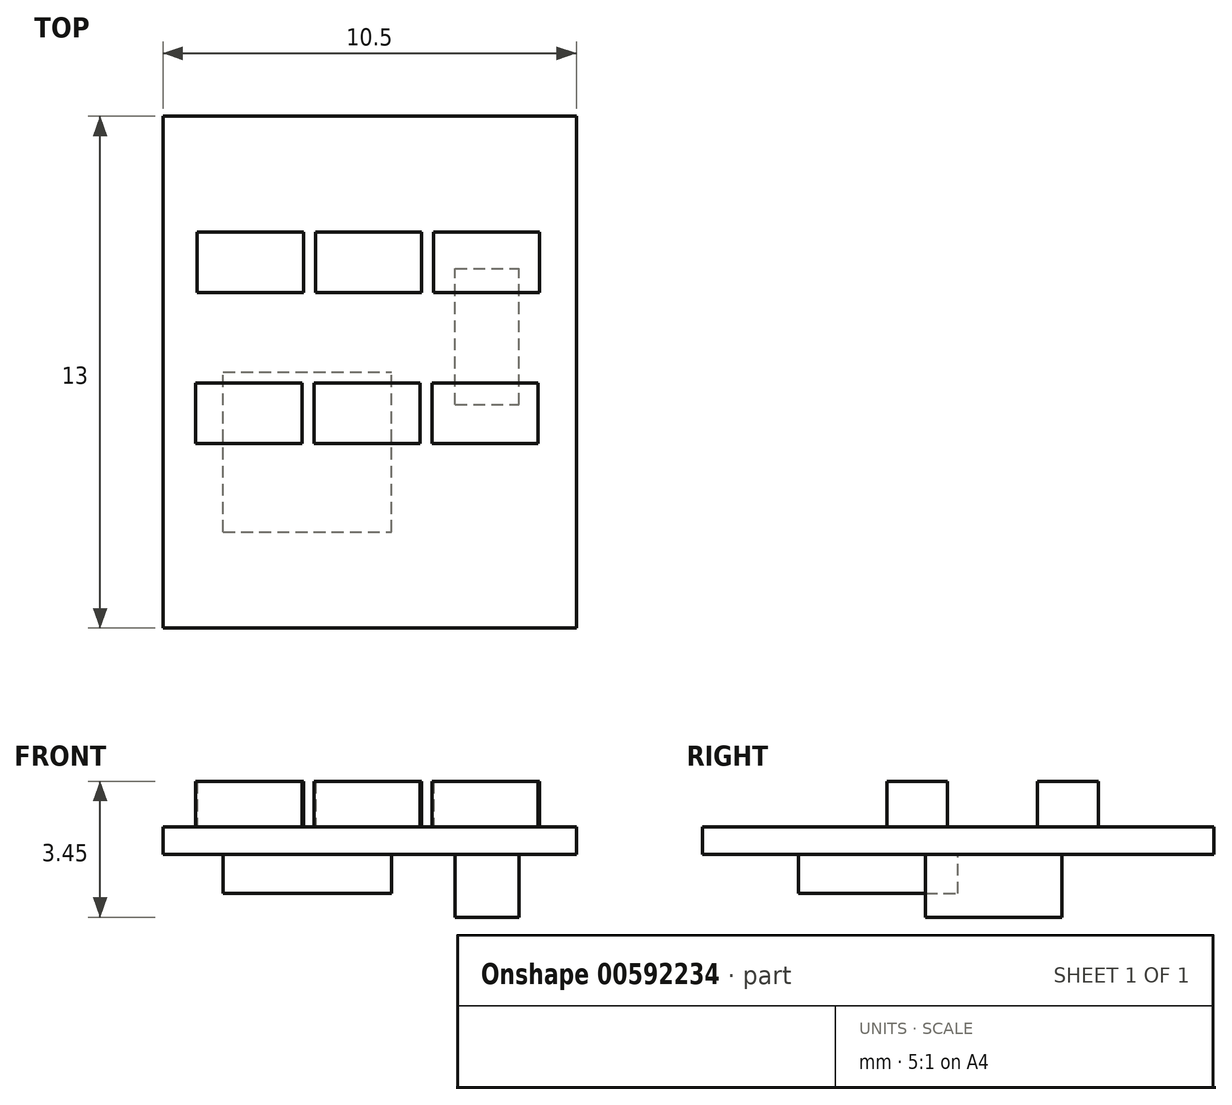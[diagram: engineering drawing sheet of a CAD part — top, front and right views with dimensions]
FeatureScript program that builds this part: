
annotation { "Feature Type Name" : "Feature", "Feature Type Description" : "" }
export const myFeature = defineFeature(function(context is Context, id is Id, definition is map)
    precondition{}
    {
        {
            var Q0;
            Q0=qCreatedBy(makeId("Top.planeOp"),FACE);
            var sketch = newSketch(context, id + "F0", { "sketchPlane" : qUnion([Q0])});
            skLineSegment(sketch, "E0.bottom", {"start": v(-5.25, 6.5) * mm, "end": v(5.25, 6.5) * mm});
            skLineSegment(sketch, "E0.top", {"start": v(-5.25, -6.5) * mm, "end": v(5.25, -6.5) * mm});
            skLineSegment(sketch, "E0.left", {"start": v(-5.25, 6.5) * mm, "end": v(-5.25, -6.5) * mm});
            skLineSegment(sketch, "E0.right", {"start": v(5.25, 6.5) * mm, "end": v(5.25, -6.5) * mm});
            skPoint(sketch, "E0.middle", {"position": v(0, 0) * mm});
            skLineSegment(sketch, "E1.bottom", {"start": v(-4.38, 3.56) * mm, "end": v(-1.68, 3.56) * mm});
            skLineSegment(sketch, "E1.top", {"start": v(-4.38, 2.02) * mm, "end": v(-1.68, 2.02) * mm});
            skLineSegment(sketch, "E1.left", {"start": v(-4.38, 3.56) * mm, "end": v(-4.38, 2.02) * mm});
            skLineSegment(sketch, "E1.right", {"start": v(-1.68, 3.56) * mm, "end": v(-1.68, 2.02) * mm});
            skLineSegment(sketch, "E2.1.0.0", {"start": v(-1.38, 3.56) * mm, "end": v(1.32, 3.56) * mm});
            skLineSegment(sketch, "E2.1.0.1", {"start": v(-1.38, 3.56) * mm, "end": v(-1.38, 2.02) * mm});
            skLineSegment(sketch, "E2.1.0.2", {"start": v(1.32, 3.56) * mm, "end": v(1.32, 2.02) * mm});
            skLineSegment(sketch, "E2.1.0.3", {"start": v(-1.38, 2.02) * mm, "end": v(1.32, 2.02) * mm});
            skLineSegment(sketch, "E2.2.0.0", {"start": v(1.62, 3.56) * mm, "end": v(4.32, 3.56) * mm});
            skLineSegment(sketch, "E2.2.0.1", {"start": v(1.62, 3.56) * mm, "end": v(1.62, 2.02) * mm});
            skLineSegment(sketch, "E2.2.0.2", {"start": v(4.32, 3.56) * mm, "end": v(4.32, 2.02) * mm});
            skLineSegment(sketch, "E2.2.0.3", {"start": v(1.62, 2.02) * mm, "end": v(4.32, 2.02) * mm});
            skLineSegment(sketch, "E2.direction1", {"start": v(-4.38, 3.56) * mm, "end": v(-1.38, 3.56) * mm, "construction": true});
            skLineSegment(sketch, "E3.1.0.0", {"start": v(-4.42, -0.27) * mm, "end": v(-4.42, -1.81) * mm});
            skLineSegment(sketch, "E3.1.0.1", {"start": v(-4.42, -1.81) * mm, "end": v(-1.72, -1.81) * mm});
            skLineSegment(sketch, "E3.1.0.2", {"start": v(4.28, -0.27) * mm, "end": v(4.28, -1.81) * mm});
            skLineSegment(sketch, "E3.1.0.3", {"start": v(1.58, -1.81) * mm, "end": v(4.28, -1.81) * mm});
            skLineSegment(sketch, "E3.1.0.4", {"start": v(1.58, -0.27) * mm, "end": v(1.58, -1.81) * mm});
            skLineSegment(sketch, "E3.1.0.5", {"start": v(-1.72, -0.27) * mm, "end": v(-1.72, -1.81) * mm});
            skLineSegment(sketch, "E3.1.0.6", {"start": v(-1.42, -0.27) * mm, "end": v(1.28, -0.27) * mm});
            skLineSegment(sketch, "E3.1.0.7", {"start": v(-1.42, -0.27) * mm, "end": v(-1.42, -1.81) * mm});
            skLineSegment(sketch, "E3.1.0.8", {"start": v(1.28, -0.27) * mm, "end": v(1.28, -1.81) * mm});
            skLineSegment(sketch, "E3.1.0.9", {"start": v(-1.42, -1.81) * mm, "end": v(1.28, -1.81) * mm});
            skLineSegment(sketch, "E3.1.0.10", {"start": v(1.58, -0.27) * mm, "end": v(4.28, -0.27) * mm});
            skLineSegment(sketch, "E3.1.0.11", {"start": v(-4.42, -0.27) * mm, "end": v(-1.42, -0.27) * mm, "construction": true});
            skLineSegment(sketch, "E3.1.0.12", {"start": v(-4.42, -0.27) * mm, "end": v(-1.72, -0.27) * mm});
            skLineSegment(sketch, "E3.direction1", {"start": v(-4.38, 2.02) * mm, "end": v(-4.42, -1.81) * mm, "construction": true});
            skSolve(sketch);
        }
        {
            var Q0;
            Q0=makeQuery(id+"F0.imprint","IMPRINT",FACE,{"disambiguationData":[TD([[makeQuery(id+"F0.imprint","IMPRINT",EDGE,{"derivedFrom":sQuery(id+"F0.wireOp",EDGE,"E0.bottom")}),-1.0]])]});
            var Q1;
            Q1=makeQuery(id+"F0.imprint","IMPRINT",FACE,{"disambiguationData":[TD([[makeQuery(id+"F0.imprint","IMPRINT",EDGE,{"derivedFrom":sQuery(id+"F0.wireOp",EDGE,"E3.1.0.0")}),1.0]])]});
            var Q2;
            Q2=makeQuery(id+"F0.imprint","IMPRINT",FACE,{"disambiguationData":[TD([[makeQuery(id+"F0.imprint","IMPRINT",EDGE,{"derivedFrom":sQuery(id+"F0.wireOp",EDGE,"E1.bottom")}),-1.0]])]});
            var Q3;
            Q3=makeQuery(id+"F0.imprint","IMPRINT",FACE,{"disambiguationData":[TD([[makeQuery(id+"F0.imprint","IMPRINT",EDGE,{"derivedFrom":sQuery(id+"F0.wireOp",EDGE,"E2.1.0.0")}),-1.0]])]});
            var Q4;
            Q4=makeQuery(id+"F0.imprint","IMPRINT",FACE,{"disambiguationData":[TD([[makeQuery(id+"F0.imprint","IMPRINT",EDGE,{"derivedFrom":sQuery(id+"F0.wireOp",EDGE,"E3.1.0.6")}),-1.0]])]});
            var Q5;
            Q5=makeQuery(id+"F0.imprint","IMPRINT",FACE,{"disambiguationData":[TD([[makeQuery(id+"F0.imprint","IMPRINT",EDGE,{"derivedFrom":sQuery(id+"F0.wireOp",EDGE,"E3.1.0.2")}),-1.0]])]});
            var Q6;
            Q6=makeQuery(id+"F0.imprint","IMPRINT",FACE,{"disambiguationData":[TD([[makeQuery(id+"F0.imprint","IMPRINT",EDGE,{"derivedFrom":sQuery(id+"F0.wireOp",EDGE,"E2.2.0.0")}),-1.0]])]});
            extrude(context, id + "F1", {"entities" : qUnion([Q0, Q1, Q2, Q3, Q4, Q5, Q6]), "depth" : 0.7 * mm, "offsetDistance" : 25 * mm});
        }
        {
            var Q0;
            Q0=makeQuery(id+"F0.imprint","IMPRINT",FACE,{"disambiguationData":[TD([[makeQuery(id+"F0.imprint","IMPRINT",EDGE,{"derivedFrom":sQuery(id+"F0.wireOp",EDGE,"E3.1.0.0")}),1.0]])]});
            var Q1;
            Q1=makeQuery(id+"F0.imprint","IMPRINT",FACE,{"disambiguationData":[TD([[makeQuery(id+"F0.imprint","IMPRINT",EDGE,{"derivedFrom":sQuery(id+"F0.wireOp",EDGE,"E3.1.0.6")}),-1.0]])]});
            var Q2;
            Q2=makeQuery(id+"F0.imprint","IMPRINT",FACE,{"disambiguationData":[TD([[makeQuery(id+"F0.imprint","IMPRINT",EDGE,{"derivedFrom":sQuery(id+"F0.wireOp",EDGE,"E3.1.0.2")}),-1.0]])]});
            var Q3;
            Q3=makeQuery(id+"F0.imprint","IMPRINT",FACE,{"disambiguationData":[TD([[makeQuery(id+"F0.imprint","IMPRINT",EDGE,{"derivedFrom":sQuery(id+"F0.wireOp",EDGE,"E2.2.0.0")}),-1.0]])]});
            var Q4;
            Q4=makeQuery(id+"F0.imprint","IMPRINT",FACE,{"disambiguationData":[TD([[makeQuery(id+"F0.imprint","IMPRINT",EDGE,{"derivedFrom":sQuery(id+"F0.wireOp",EDGE,"E2.1.0.0")}),-1.0]])]});
            var Q5;
            Q5=makeQuery(id+"F0.imprint","IMPRINT",FACE,{"disambiguationData":[TD([[makeQuery(id+"F0.imprint","IMPRINT",EDGE,{"derivedFrom":sQuery(id+"F0.wireOp",EDGE,"E1.bottom")}),-1.0]])]});
            extrude(context, id + "F2", {"entities" : qUnion([Q0, Q1, Q2, Q3, Q4, Q5]), "operationType" : NewBodyOperationType.ADD, "depth" : 1.85 * mm, "offsetDistance" : 25 * mm});
        }
        {
            var Q0;
            Q0=makeQuery(id+"F0.imprint","IMPRINT",FACE,{"disambiguationData":[TD([[makeQuery(id+"F0.imprint","IMPRINT",EDGE,{"derivedFrom":sQuery(id+"F0.wireOp",EDGE,"E0.bottom")}),-1.0]])]});
            var sketch = newSketch(context, id + "F3", { "sketchPlane" : qUnion([Q0])});
            skLineSegment(sketch, "E4.bottom", {"start": v(-3.72, -4.06) * mm, "end": v(0.56, -4.06) * mm});
            skLineSegment(sketch, "E4.top", {"start": v(-3.72, 0) * mm, "end": v(0.56, 0) * mm});
            skLineSegment(sketch, "E4.left", {"start": v(-3.72, -4.06) * mm, "end": v(-3.72, 0) * mm});
            skLineSegment(sketch, "E4.right", {"start": v(0.56, -4.06) * mm, "end": v(0.56, 0) * mm});
            skLineSegment(sketch, "E5.bottom", {"start": v(2.17, -0.83) * mm, "end": v(3.8, -0.83) * mm});
            skLineSegment(sketch, "E5.top", {"start": v(2.17, 2.63) * mm, "end": v(3.8, 2.63) * mm});
            skLineSegment(sketch, "E5.left", {"start": v(2.17, -0.83) * mm, "end": v(2.17, 2.63) * mm});
            skLineSegment(sketch, "E5.right", {"start": v(3.8, -0.83) * mm, "end": v(3.8, 2.63) * mm});
            skSolve(sketch);
        }
        {
            var Q0;
            {var subQ9=sQuery(id+"F3.wireOp",EDGE,"E4.bottom");Q0=makeQuery(id+"F3.imprint","IMPRINT",FACE,{"disambiguationData":[TD([[makeQuery(id+"F3.imprint","IMPRINT",EDGE,{"derivedFrom":subQ9}),1.0]])]});}
            var Q1;
            {var subQ5=makeQuery(id+"F0.imprint","IMPRINT",EDGE,{"derivedFrom":sQuery(id+"F0.wireOp",EDGE,"E3.1.0.7")});Q1=makeQuery(id+"F3.imprint","IMPRINT",FACE,{"disambiguationData":[TD([[makeQuery(id+"F3.imprint","IMPRINT",EDGE,{"derivedFrom":subQ5}),1.0]])]});}
            var Q2;
            {var subQ5=makeQuery(id+"F0.imprint","IMPRINT",EDGE,{"derivedFrom":sQuery(id+"F0.wireOp",EDGE,"E3.1.0.5")});Q2=makeQuery(id+"F3.imprint","IMPRINT",FACE,{"disambiguationData":[TD([[makeQuery(id+"F3.imprint","IMPRINT",EDGE,{"derivedFrom":subQ5}),-1.0]])]});}
            extrude(context, id + "F4", {"entities" : qUnion([Q0, Q1, Q2]), "operationType" : NewBodyOperationType.ADD, "oppositeDirection" : true, "depth" : 1 * mm, "offsetDistance" : 25 * mm});
        }
        {
            var Q0;
            {var subQ0=sQuery(id+"F3.wireOp",EDGE,"E5.bottom");Q0=makeQuery(id+"F3.imprint","IMPRINT",FACE,{"disambiguationData":[TD([[makeQuery(id+"F3.imprint","IMPRINT",EDGE,{"derivedFrom":subQ0}),1.0]])]});}
            var Q1;
            {var subQ0=sQuery(id+"F3.wireOp",EDGE,"E5.left");var subQ1=makeQuery(id+"F0.imprint","IMPRINT",EDGE,{"derivedFrom":sQuery(id+"F0.wireOp",EDGE,"E3.1.0.10")});var subQ2=makeQuery(id+"F3.imprint","INTERSECT",VERTEX,{"derivedFrom":[subQ1,subQ0]});Q1=makeQuery(id+"F3.imprint","IMPRINT",FACE,{"disambiguationData":[TD([[makeQuery(id+"F3.imprint","IMPRINT",EDGE,{"disambiguationData":[TD([[subQ2,-1.0]])],"derivedFrom":subQ0}),-1.0]])]});}
            var Q2;
            {var subQ0=sQuery(id+"F3.wireOp",EDGE,"E5.top");Q2=makeQuery(id+"F3.imprint","IMPRINT",FACE,{"disambiguationData":[TD([[makeQuery(id+"F3.imprint","IMPRINT",EDGE,{"derivedFrom":subQ0}),-1.0]])]});}
            extrude(context, id + "F5", {"entities" : qUnion([Q0, Q1, Q2]), "operationType" : NewBodyOperationType.ADD, "oppositeDirection" : true, "depth" : 1.6 * mm, "offsetDistance" : 25 * mm});
        }
    });
